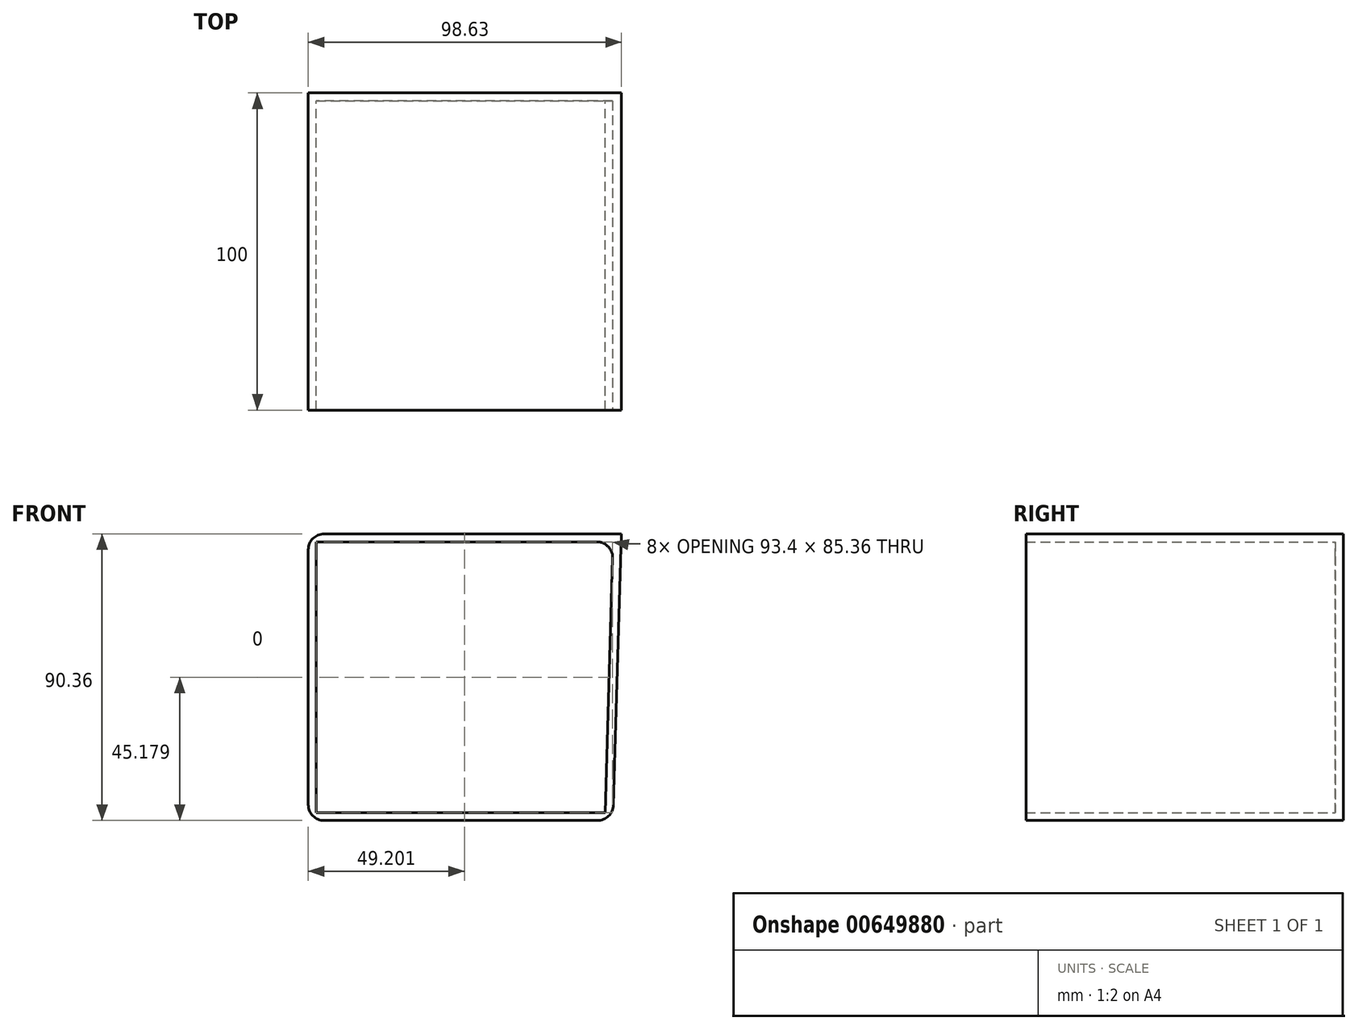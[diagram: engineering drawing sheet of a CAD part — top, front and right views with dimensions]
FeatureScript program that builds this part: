
annotation { "Feature Type Name" : "Feature", "Feature Type Description" : "" }
export const myFeature = defineFeature(function(context is Context, id is Id, definition is map)
    precondition{}
    {
        {
            var Q0;
            Q0=qCreatedBy(makeId("Front.planeOp"),FACE);
            var sketch = newSketch(context, id + "F0", { "sketchPlane" : qUnion([Q0])});
            skLineSegment(sketch, "E0", {"start": v(49.99, 55.12) * mm, "end": v(-48.64, 55.12) * mm});
            skLineSegment(sketch, "E1", {"start": v(-48.64, 55.12) * mm, "end": v(-48.64, -35.24) * mm});
            skLineSegment(sketch, "E2", {"start": v(-48.64, -35.24) * mm, "end": v(47.31, -35.24) * mm});
            skLineSegment(sketch, "E3", {"start": v(47.31, -35.24) * mm, "end": v(49.99, 55.12) * mm});
            skSolve(sketch);
        }
        {
            var Q0;
            Q0=makeQuery(id+"F0.imprint","IMPRINT",FACE,{"disambiguationData":[TD([[makeQuery(id+"F0.imprint","IMPRINT",EDGE,{"derivedFrom":sQuery(id+"F0.wireOp",EDGE,"E0")}),1.0]])]});
            extrude(context, id + "F1", {"entities" : qUnion([Q0]), "depth" : 100 * mm, "offsetDistance" : 25 * mm});
        }
        {
            var Q0;
            Q0=makeQuery(id+"F1.opExtrude","CAP_FACE",FACE,{"disambiguationData":[OSD([sQuery(id+"F0.wireOp",EDGE,"E0"),sQuery(id+"F0.wireOp",EDGE,"E1"),sQuery(id+"F0.wireOp",EDGE,"E2"),sQuery(id+"F0.wireOp",EDGE,"E3")])],"isStart":false});
            shell(context, id + "F2", {"entities" : qUnion([Q0]), "thickness" : 2.5 * mm});
        }
        {
            var Q0;
            Q0=makeQuery(id+"F1.opExtrude","SWEPT_EDGE",EDGE,{"disambiguationData":[OSD([sQuery(id+"F0.wireOp",EDGE,"E0"),sQuery(id+"F0.wireOp",EDGE,"E1")])]});
            var Q1;
            Q1=makeQuery(id+"F2.opShell","OFFSET_EDGE",EDGE,{"disambiguationData":[OSD([sQuery(id+"F0.wireOp",EDGE,"E0"),sQuery(id+"F0.wireOp",EDGE,"E3")])]});
            var Q2;
            Q2=makeQuery(id+"F1.opExtrude","SWEPT_EDGE",EDGE,{"disambiguationData":[OSD([sQuery(id+"F0.wireOp",EDGE,"E1"),sQuery(id+"F0.wireOp",EDGE,"E2")])]});
            var Q3;
            Q3=makeQuery(id+"F1.opExtrude","SWEPT_EDGE",EDGE,{"disambiguationData":[OSD([sQuery(id+"F0.wireOp",EDGE,"E2"),sQuery(id+"F0.wireOp",EDGE,"E3")])]});
            fillet(context, id + "F3", {"entities" : qUnion([Q0, Q1, Q2, Q3]), "radius" : 5 * mm, "tangentPropagation" : true, "allowEdgeOverflow" : false});
        }
    });
